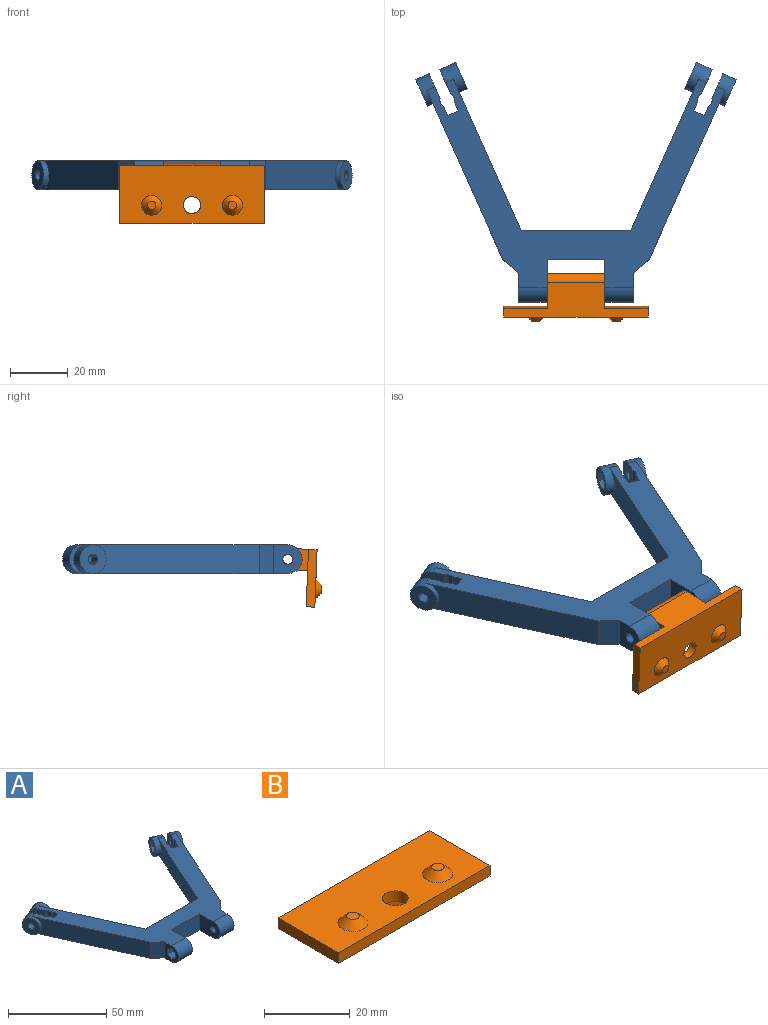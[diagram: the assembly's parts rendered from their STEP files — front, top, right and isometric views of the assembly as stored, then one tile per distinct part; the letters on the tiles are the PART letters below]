
ASSEMBLY  parts=2 mates=1
PART A: 65 faces, bbox 111.2x83.2x10 mm
  f0: plane 10x10mm, normal (-1,0,0), area 62.1mm2, adj f12,f16,f17,f30,f58,f59,f60,f61
  f1: cylinder r=1.75mm len=6mm, axis (-1,0,0), area 66mm2, adj f13,f64
  f2: cylinder r=1.75mm len=4.42mm, axis (-0.91,-0.41,0), area 33mm2, adj f3,f29
  f3: plane 10x8.42mm, normal (-0.91,-0.41,0), area 72mm2, adj f2,f6,f16,f17,f21
  f4: plane 10x8.58mm, normal (0.91,0.41,0), area 73.6mm2, adj f10,f16,f17,f19,f22
  f5: plane 52.48x23.53mm, normal (0.91,0.41,0), area 535.9mm2, adj f15,f16,f17,f21
  f6: cylinder r=2.5mm len=10mm, axis (0,0,-1), area 32.2mm2, adj f3,f7,f16,f17
  f7: plane 10x3.19mm, normal (-0.91,-0.41,0), area 35mm2, adj f6,f8,f16,f17
  f8: plane 10x3.65mm, normal (-0.41,0.91,0), area 40mm2, adj f7,f9,f16,f17
  f9: plane 10x3.19mm, normal (0.91,0.41,0), area 35mm2, adj f8,f10,f16,f17
  f10: cylinder r=2.5mm len=10mm, axis (0,0,-1), area 32.2mm2, adj f4,f9,f16,f17
  f11: plane 58.5x26.23mm, normal (-0.91,-0.41,0), area 601.9mm2, adj f12,f16,f17,f19
  f12: plane 10x5.49mm, normal (-0.67,-0.74,0), area 74.3mm2, adj f0,f11,f16,f17
  f13: plane 15x10mm, normal (1,0,0), area 129.6mm2, adj f1,f14,f16,f17,f30
  f14: plane 20x10mm, normal (0,-1,0), area 200mm2, adj f13,f16,f17,f43
  f15: plane 38x10mm, normal (0,1,0), area 380mm2, adj f5,f16,f17,f34
  f16: plane 103.45x72.44mm, normal (0,0,1), area 1796.3mm2, adj f0,f3,f4,f5,f6,f7,f8,f9
  f17: plane 103.45x72.44mm, normal (0,0,-1), area 1796.3mm2, adj f0,f3,f4,f5,f6,f7,f8,f9
  f18: plane 10x9.12mm, normal (-0.91,-0.41,0), area 68.9mm2, adj f19,f22
  f19: cylinder r=5mm len=11.17mm, axis (0.91,0.41,0), area 110mm2, adj f4,f11,f16,f17,f18
  f20: plane 10x9.12mm, normal (0.91,0.41,0), area 51.4mm2, adj f21,f23,f24,f25,f26,f27,f28
  f21: cylinder r=5mm len=11.58mm, axis (-0.91,-0.41,0), area 141.4mm2, adj f3,f5,f16,f17,f20
  f22: cylinder r=1.75mm len=5.99mm, axis (0.91,0.41,0), area 55mm2, adj f4,f18
  f23: plane 3.23x2.74mm, normal (0.41,-0.91,0), area 9.7mm2, adj f20,f24,f28,f29
  f24: plane 3.88x3.78mm, normal (0.2,-0.46,-0.87), area 9.7mm2, adj f20,f23,f25,f29
  f25: plane 3.88x3.78mm, normal (-0.2,0.46,-0.87), area 9.7mm2, adj f20,f24,f26,f29
  f26: plane 3.23x2.74mm, normal (-0.41,0.91,0), area 9.7mm2, adj f20,f25,f27,f29
  f27: plane 3.88x3.78mm, normal (-0.2,0.46,0.87), area 9.7mm2, adj f20,f26,f28,f29
  f28: plane 3.88x3.78mm, normal (0.2,-0.46,0.87), area 9.7mm2, adj f20,f23,f27,f29
  f29: plane 6.47x5.11mm, normal (0.91,0.41,0), area 17.5mm2, adj f2,f23,f24,f25,f26,f27,f28
  f30: cylinder r=5mm len=10mm, axis (-1,0,0), area 157.1mm2, adj f0,f13,f16,f17
  f31: cylinder r=1.75mm len=4.42mm, axis (0.91,-0.41,0), area 33mm2, adj f32,f55
  f32: plane 10x8.42mm, normal (0.91,-0.41,0), area 72mm2, adj f16,f17,f31,f35,f47
  f33: plane 10x8.58mm, normal (-0.91,0.41,0), area 73.6mm2, adj f16,f17,f39,f45,f48
  f34: plane 52.48x23.53mm, normal (-0.91,0.41,0), area 535.9mm2, adj f15,f16,f17,f47
  f35: cylinder r=2.5mm len=10mm, axis (0,0,-1), area 32.2mm2, adj f16,f17,f32,f36
  f36: plane 10x3.19mm, normal (0.91,-0.41,0), area 35mm2, adj f16,f17,f35,f37
  f37: plane 10x3.65mm, normal (0.41,0.91,0), area 40mm2, adj f16,f17,f36,f38
  f38: plane 10x3.19mm, normal (-0.91,0.41,0), area 35mm2, adj f16,f17,f37,f39
  f39: cylinder r=2.5mm len=10mm, axis (0,0,-1), area 32.2mm2, adj f16,f17,f33,f38
  f40: plane 58.5x26.23mm, normal (0.91,-0.41,0), area 601.9mm2, adj f16,f17,f41,f45
  f41: plane 10x5.49mm, normal (0.67,-0.74,0), area 74.3mm2, adj f16,f17,f40,f42
  f42: plane 10x10mm, normal (1,0,0), area 79.6mm2, adj f16,f17,f41,f56,f57
  f43: plane 15x10mm, normal (-1,0,0), area 129.6mm2, adj f14,f16,f17,f56,f57
  f44: plane 10x9.12mm, normal (0.91,-0.41,0), area 68.9mm2, adj f45,f48
  f45: cylinder r=5mm len=11.17mm, axis (-0.91,0.41,0), area 110mm2, adj f16,f17,f33,f40,f44
  f46: plane 10x9.12mm, normal (-0.91,0.41,0), area 51.4mm2, adj f47,f49,f50,f51,f52,f53,f54
  f47: cylinder r=5mm len=11.58mm, axis (0.91,-0.41,0), area 141.4mm2, adj f16,f17,f32,f34,f46
  f48: cylinder r=1.75mm len=5.99mm, axis (-0.91,0.41,0), area 55mm2, adj f33,f44
  f49: plane 3.23x2.74mm, normal (-0.41,-0.91,0), area 9.7mm2, adj f46,f50,f54,f55
  f50: plane 3.88x3.78mm, normal (-0.2,-0.46,-0.87), area 9.7mm2, adj f46,f49,f51,f55
  f51: plane 3.88x3.78mm, normal (0.2,0.46,-0.87), area 9.7mm2, adj f46,f50,f52,f55
  f52: plane 3.23x2.74mm, normal (0.41,0.91,0), area 9.7mm2, adj f46,f51,f53,f55
  f53: plane 3.88x3.78mm, normal (0.2,0.46,0.87), area 9.7mm2, adj f46,f52,f54,f55
  f54: plane 3.88x3.78mm, normal (-0.2,-0.46,0.87), area 9.7mm2, adj f46,f49,f53,f55
  f55: plane 6.47x5.11mm, normal (-0.91,0.41,0), area 17.5mm2, adj f31,f49,f50,f51,f52,f53,f54
  f56: cylinder r=5mm len=10mm, axis (1,0,0), area 157.1mm2, adj f16,f17,f42,f43
  f57: cylinder r=1.75mm len=10mm, axis (1,0,0), area 110mm2, adj f42,f43
  f58: plane 4x2.8mm, normal (0,0.5,-0.87), area 12.9mm2, adj f0,f59,f63,f64
  f59: plane 4x2.8mm, normal (0,-0.5,-0.87), area 12.9mm2, adj f0,f58,f60,f64
  f60: plane 4x3.23mm, normal (0,-1,0), area 12.9mm2, adj f0,f59,f61,f64
  f61: plane 4x2.8mm, normal (0,-0.5,0.87), area 12.9mm2, adj f0,f60,f62,f64
  f62: plane 4x2.8mm, normal (0,0.5,0.87), area 12.9mm2, adj f0,f61,f63,f64
  f63: plane 4x3.23mm, normal (0,1,0), area 12.9mm2, adj f0,f58,f62,f64
  f64: plane 6.47x5.6mm, normal (-1,0,0), area 17.5mm2, adj f1,f58,f59,f60,f61,f62,f63
PART B: 18 faces, bbox 50x20x17 mm
  f0: plane 50x12mm, normal (0,1,0), area 330mm2, adj f4,f5,f7,f8,f9,f11,f13
  f1: plane 20x9mm, normal (0,-1,0), area 180mm2, adj f4,f5,f6,f8
  f2: cylinder r=1.75mm len=20mm, axis (-1,0,0), area 219.9mm2, adj f4,f5
  f3: plane 20x1.5mm, normal (0,0,-1), area 30mm2, adj f4,f5,f6,f7
  f4: plane 12x7.5mm, normal (1,0,0), area 76.5mm2, adj f0,f1,f2,f3,f6,f7,f8
  f5: plane 12x7.5mm, normal (-1,0,0), area 76.5mm2, adj f0,f1,f2,f3,f6,f7,f8
  f6: cylinder r=3mm len=20mm, axis (1,0,0), area 94.2mm2, adj f1,f3,f4,f5
  f7: cylinder r=3mm len=20mm, axis (1,0,0), area 94.2mm2, adj f0,f3,f4,f5
  f8: plane 50x20mm, normal (0,0,-1), area 821.7mm2, adj f0,f1,f4,f5,f9,f10,f11,f12
  f9: plane 20x3mm, normal (-1,0,0), area 60mm2, adj f0,f8,f10,f13
  f10: plane 50x3mm, normal (0,-1,0), area 150mm2, adj f8,f9,f11,f13
  f11: plane 20x3mm, normal (1,0,0), area 60mm2, adj f0,f8,f10,f13
  f12: cylinder r=3mm len=6mm, axis (0,0,-1), area 56.5mm2, adj f8,f13
  f13: plane 50x20mm, normal (0,0,1), area 894.8mm2, adj f0,f9,f10,f11,f12,f16,f17
  f14: plane 3x3mm, normal (0,0,1), area 7.1mm2, adj f17
  f15: plane 3x3mm, normal (0,0,1), area 7.1mm2, adj f16
  f16: cone r=1.5mm half-angle=45deg, axis (0,0,-1), area 44.4mm2, adj f13,f15
  f17: cone r=1.5mm half-angle=45deg, axis (0,0,-1), area 44.4mm2, adj f13,f14
PLACE A rot(axis=(0,1,0),180deg) t=(0,44.68,0)mm fixed
PLACE B rot(axis=(1,0,0),92.3deg) t=(0,29.72,0)mm
MATE revolute A.f1 <-> B.f2  axis (-1,0,0) through (10,29.72,0)mm
